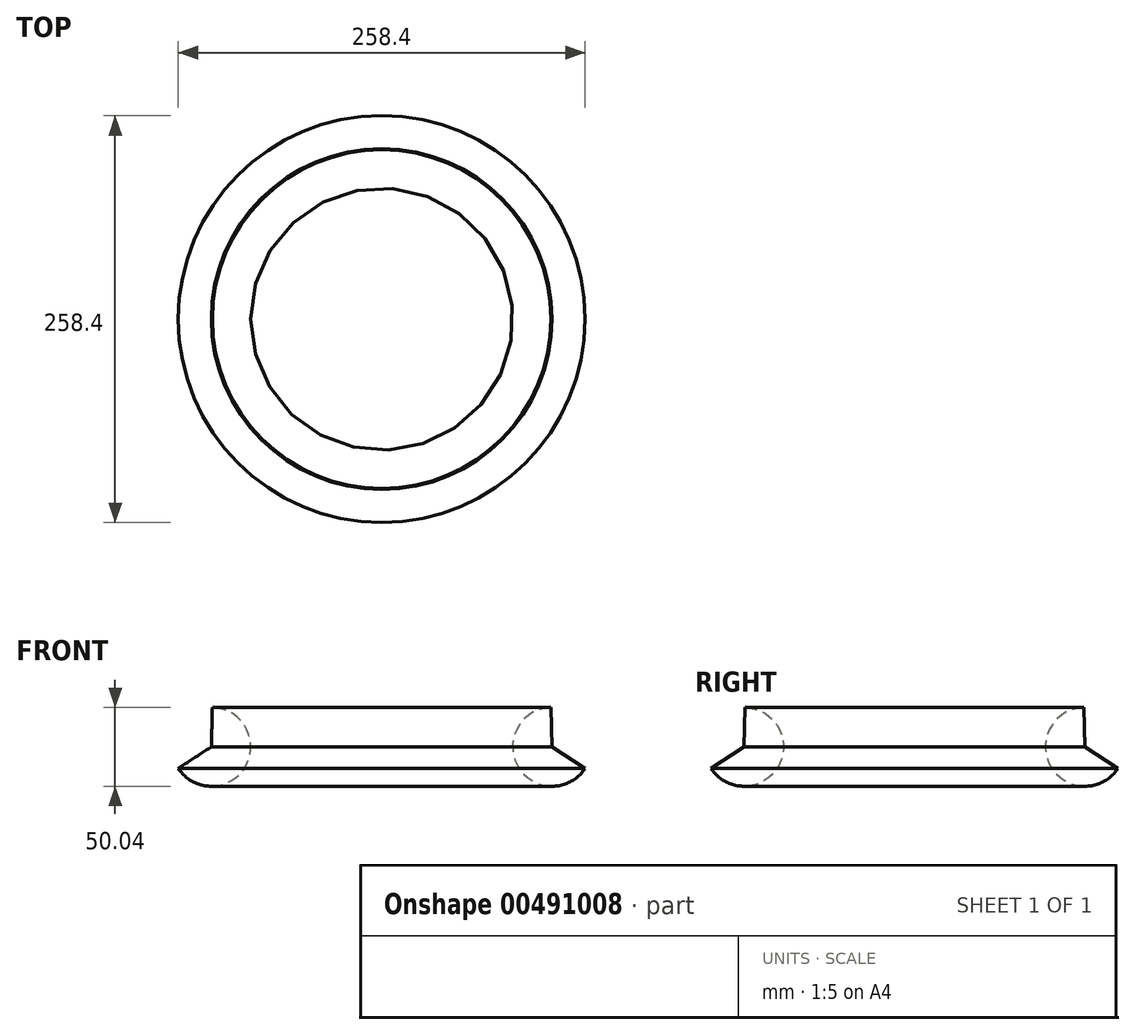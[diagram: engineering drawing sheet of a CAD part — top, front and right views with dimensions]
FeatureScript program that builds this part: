
annotation { "Feature Type Name" : "Feature", "Feature Type Description" : "" }
export const myFeature = defineFeature(function(context is Context, id is Id, definition is map)
    precondition{}
    {
        {
            var Q0;
            Q0=qCreatedBy(makeId("Front.planeOp"),FACE);
            var sketch = newSketch(context, id + "F0", { "sketchPlane" : qUnion([Q0])});
            skLineSegment(sketch, "E0", {"start": v(0, 0) * mm, "end": v(0, 51.23) * mm, "construction": true});
            skLineSegment(sketch, "E1", {"start": v(0, 0) * mm, "end": v(141.02, 0) * mm, "construction": true});
            skArc(sketch, "E2", {"start": v(107.55, 50.04) * mm, "mid": v(86.38, 12.8) * mm, "end": v(129.2, 11.4) * mm});
            skLineSegment(sketch, "E3", {"start": v(107.55, 50.04) * mm, "end": v(108.22, 25.02) * mm});
            skLineSegment(sketch, "E4", {"start": v(108.22, 25.02) * mm, "end": v(129.2, 11.4) * mm});
            skLineSegment(sketch, "E5", {"start": v(108.22, 25.02) * mm, "end": v(133, 29.52) * mm, "construction": true});
            skLineSegment(sketch, "E6", {"start": v(107.55, 50.04) * mm, "end": v(127.32, 28.49) * mm, "construction": true});
            skLineSegment(sketch, "E7", {"start": v(127.32, 28.49) * mm, "end": v(127.32, 12.62) * mm, "construction": true});
            skSolve(sketch);
        }
        {
            var Q0;
            Q0 = qSketchRegion(id + "F0", true);
            var Q1;
            Q1=sQuery(id+"F0.wireOp",EDGE,"E0");
            revolve(context, id + "F1", {"entities" : qUnion([Q0]), "axis" : qUnion([Q1]), "revolveType" : RevolveType.FULL});
        }
    });
